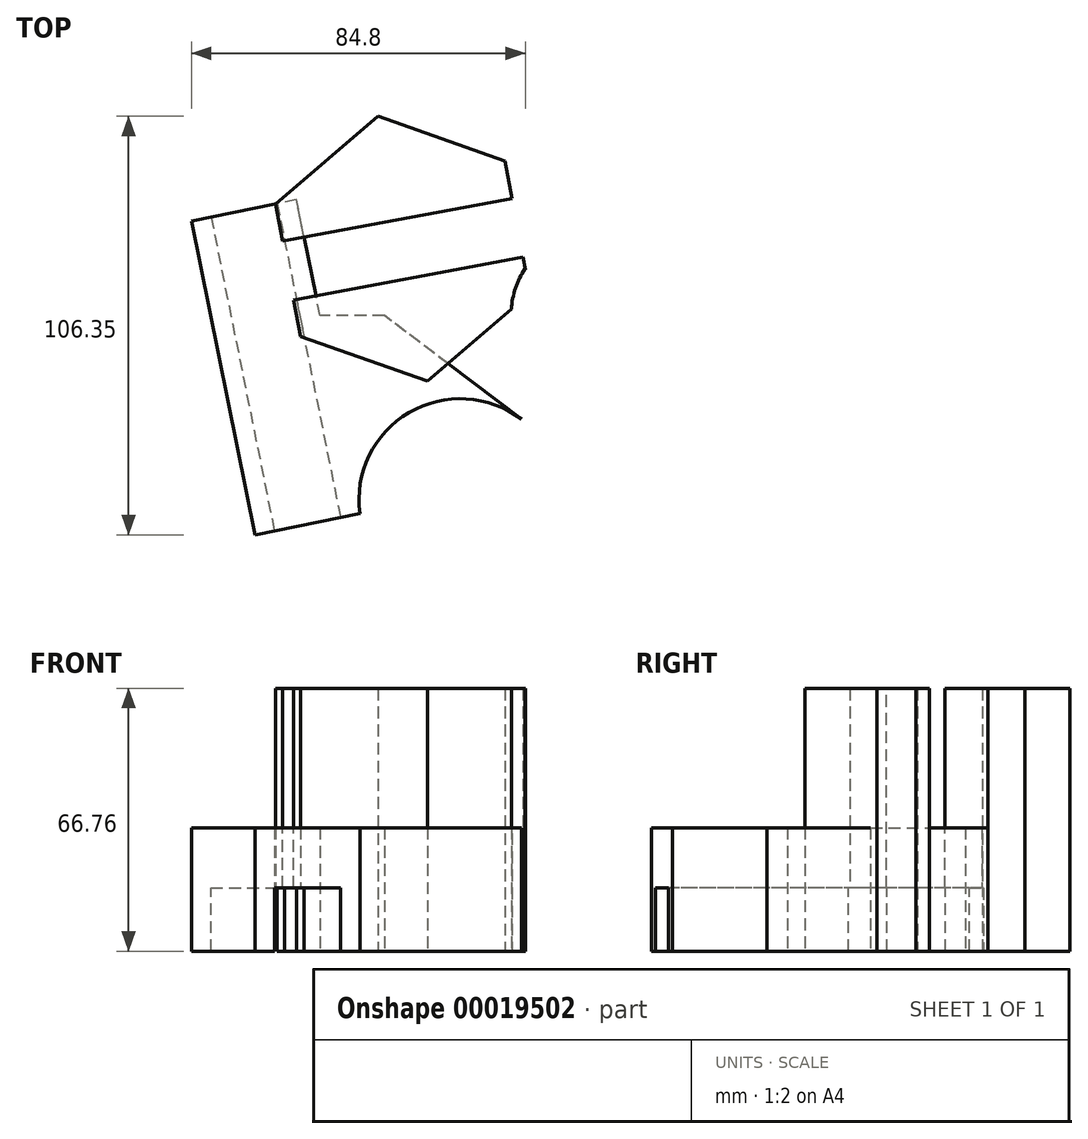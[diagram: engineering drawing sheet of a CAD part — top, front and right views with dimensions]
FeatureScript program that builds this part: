
annotation { "Feature Type Name" : "Feature", "Feature Type Description" : "" }
export const myFeature = defineFeature(function(context is Context, id is Id, definition is map)
    precondition{}
    {
        {
            var Q0;
            Q0=qCreatedBy(makeId("Front.planeOp"),FACE);
            var sketch = newSketch(context, id + "F0", { "sketchPlane" : qUnion([Q0])});
            skLineSegment(sketch, "E0", {"start": v(21.69, 0) * mm, "end": v(21.69, 39.81) * mm});
            skLineSegment(sketch, "E1", {"start": v(59.1, 0) * mm, "end": v(59.1, 39.81) * mm});
            skLineSegment(sketch, "E2", {"start": v(59.1, 0) * mm, "end": v(21.69, 0) * mm});
            skArc(sketch, "E3", {"start": v(59.1, 39.81) * mm, "mid": v(40.4, 45.26) * mm, "end": v(21.69, 39.81) * mm});
            skLineSegment(sketch, "E4", {"start": v(0, 0) * mm, "end": v(0, 52.14) * mm, "construction": true});
            skSolve(sketch);
        }
        {
            var Q0;
            Q0 = qConstructionFilter(qBodyType(qCreatedBy(id + "F0" ,EDGE), BodyType.WIRE), ConstructionObject.NO);
            var Q1;
            Q1=sQuery(id+"F0.wireOp",EDGE,"E4");
            revolve(context, id + "F1", {"bodyType" : ToolBodyType.SURFACE, "surfaceEntities" : qUnion([Q0]), "axis" : qUnion([Q1]), "revolveType" : RevolveType.FULL});
        }
        {
            var Q0;
            Q0=qCreatedBy(makeId("Top.planeOp"),FACE);
            var sketch = newSketch(context, id + "F2", { "sketchPlane" : qUnion([Q0])});
            skCircle(sketch, "E5.cCircle", {"center": v(-49.2, 17.02) * mm, "radius": 29.63 * mm, "construction": true});
            skLineSegment(sketch, "E5.0", {"start": v(-81.46, 28.4) * mm, "end": v(-55.47, 50.65) * mm});
            skLineSegment(sketch, "E5.1", {"start": v(-55.47, 50.65) * mm, "end": v(-23.2, 39.27) * mm});
            skLineSegment(sketch, "E5.2", {"start": v(-23.2, 39.27) * mm, "end": v(-16.92, 5.64) * mm});
            skLineSegment(sketch, "E5.3", {"start": v(-16.92, 5.64) * mm, "end": v(-42.91, -16.62) * mm});
            skLineSegment(sketch, "E5.4", {"start": v(-42.91, -16.62) * mm, "end": v(-75.18, -5.24) * mm});
            skLineSegment(sketch, "E5.5", {"start": v(-75.18, -5.24) * mm, "end": v(-81.46, 28.4) * mm});
            skPoint(sketch, "E5.0.midPoint", {"position": v(-68.47, 39.53) * mm});
            skSolve(sketch);
        }
        {
            var Q0;
            Q0 = qSketchRegion(id + "F2", true);
            extrude(context, id + "F3", {"entities" : qUnion([Q0]), "depth" : 66.76 * mm});
        }
        {
            var Q0;
            Q0=qCreatedBy(makeId("Top.planeOp"),FACE);
            var sketch = newSketch(context, id + "F4", { "sketchPlane" : qUnion([Q0])});
            skArc(sketch, "E6", {"start": v(-18.15, 11.94) * mm, "mid": v(-20.54, 6.98) * mm, "end": v(-21.6, 1.59) * mm});
            skLineSegment(sketch, "E7", {"start": v(-21.6, 1.59) * mm, "end": v(-15.6, 4.15) * mm});
            skLineSegment(sketch, "E8", {"start": v(-15.6, 4.15) * mm, "end": v(-18.15, 11.94) * mm});
            skSolve(sketch);
        }
        {
            var Q0;
            Q0=makeQuery(id+"F4.imprint","IMPRINT",FACE,{"disambiguationData":[TD([[makeQuery(id+"F4.imprint","IMPRINT",EDGE,{"derivedFrom":sQuery(id+"F4.wireOp",EDGE,"E6")}),1.0]])]});
            extrude(context, id + "F5", {"entities" : qUnion([Q0]), "operationType" : NewBodyOperationType.REMOVE, "depth" : 77.76 * mm});
        }
        {
            var Q0;
            Q0=makeQuery(id+"F3.opExtrude","SWEPT_FACE",FACE,{"disambiguationData":[OSD([sQuery(id+"F2.wireOp",EDGE,"E5.5")])]});
            var sketch = newSketch(context, id + "F6", { "sketchPlane" : qUnion([Q0])});
            skLineSegment(sketch, "E9.bottom", {"start": v(-33.2, 0) * mm, "end": v(-18.07, 0) * mm});
            skLineSegment(sketch, "E9.top", {"start": v(-33.2, 66.76) * mm, "end": v(-18.07, 66.76) * mm});
            skLineSegment(sketch, "E9.left", {"start": v(-33.2, 0) * mm, "end": v(-33.2, 66.76) * mm});
            skLineSegment(sketch, "E9.right", {"start": v(-18.07, 0) * mm, "end": v(-18.07, 66.76) * mm});
            skSolve(sketch);
        }
        {
            var Q0;
            Q0 = qSketchRegion(id + "F6", true);
            extrude(context, id + "F7", {"entities" : qUnion([Q0]), "operationType" : NewBodyOperationType.REMOVE, "oppositeDirection" : true, "depth" : 60.5 * mm});
        }
        {
            var Q0;
            Q0=qCreatedBy(makeId("Top.planeOp"),FACE);
            var sketch = newSketch(context, id + "F8", { "sketchPlane" : qUnion([Q0])});
            skLineSegment(sketch, "E10", {"start": v(-81.74, 28.35) * mm, "end": v(-102.83, 24.1) * mm});
            skLineSegment(sketch, "E11", {"start": v(-102.83, 24.1) * mm, "end": v(-86.72, -55.7) * mm});
            skLineSegment(sketch, "E12", {"start": v(-86.72, -55.7) * mm, "end": v(-60.06, -50.31) * mm});
            skLineSegment(sketch, "E13", {"start": v(-60.06, -50.31) * mm, "end": v(-76.18, 29.54) * mm});
            skLineSegment(sketch, "E14", {"start": v(-76.18, 29.54) * mm, "end": v(-81.74, 28.35) * mm});
            skArc(sketch, "E15", {"start": v(-19.03, -26.3) * mm, "mid": v(-47.56, -24.62) * mm, "end": v(-60.06, -50.31) * mm});
            skLineSegment(sketch, "E16", {"start": v(-19.03, -26.3) * mm, "end": v(-53.83, 0) * mm});
            skLineSegment(sketch, "E17", {"start": v(-53.83, 0) * mm, "end": v(-70.21, 0) * mm});
            skSolve(sketch);
        }
        {
            var Q0;
            Q0 = qSketchRegion(id + "F8", true);
            extrude(context, id + "F9", {"entities" : qUnion([Q0]), "depth" : 31.34 * mm});
        }
        {
            var Q0;
            Q0=makeQuery(id+"F9.opExtrude","SWEPT_FACE",FACE,{"disambiguationData":[OSD([sQuery(id+"F8.wireOp",EDGE,"E12")])]});
            var sketch = newSketch(context, id + "F10", { "sketchPlane" : qUnion([Q0])});
            skLineSegment(sketch, "E18.bottom", {"start": v(-91, 0) * mm, "end": v(-73.85, 0) * mm});
            skLineSegment(sketch, "E18.top", {"start": v(-91, 16.09) * mm, "end": v(-73.85, 16.09) * mm});
            skLineSegment(sketch, "E18.left", {"start": v(-91, 0) * mm, "end": v(-91, 16.09) * mm});
            skLineSegment(sketch, "E18.right", {"start": v(-73.85, 0) * mm, "end": v(-73.85, 16.09) * mm});
            skSolve(sketch);
        }
        {
            var Q0;
            Q0=makeQuery(id+"F10.imprint","IMPRINT",FACE,{"disambiguationData":[TD([[makeQuery(id+"F10.imprint","IMPRINT",EDGE,{"derivedFrom":sQuery(id+"F10.wireOp",EDGE,"E18.bottom")}),1.0]])]});
            extrude(context, id + "F11", {"entities" : qUnion([Q0]), "operationType" : NewBodyOperationType.REMOVE, "oppositeDirection" : true, "depth" : 86.2 * mm});
        }
    });
